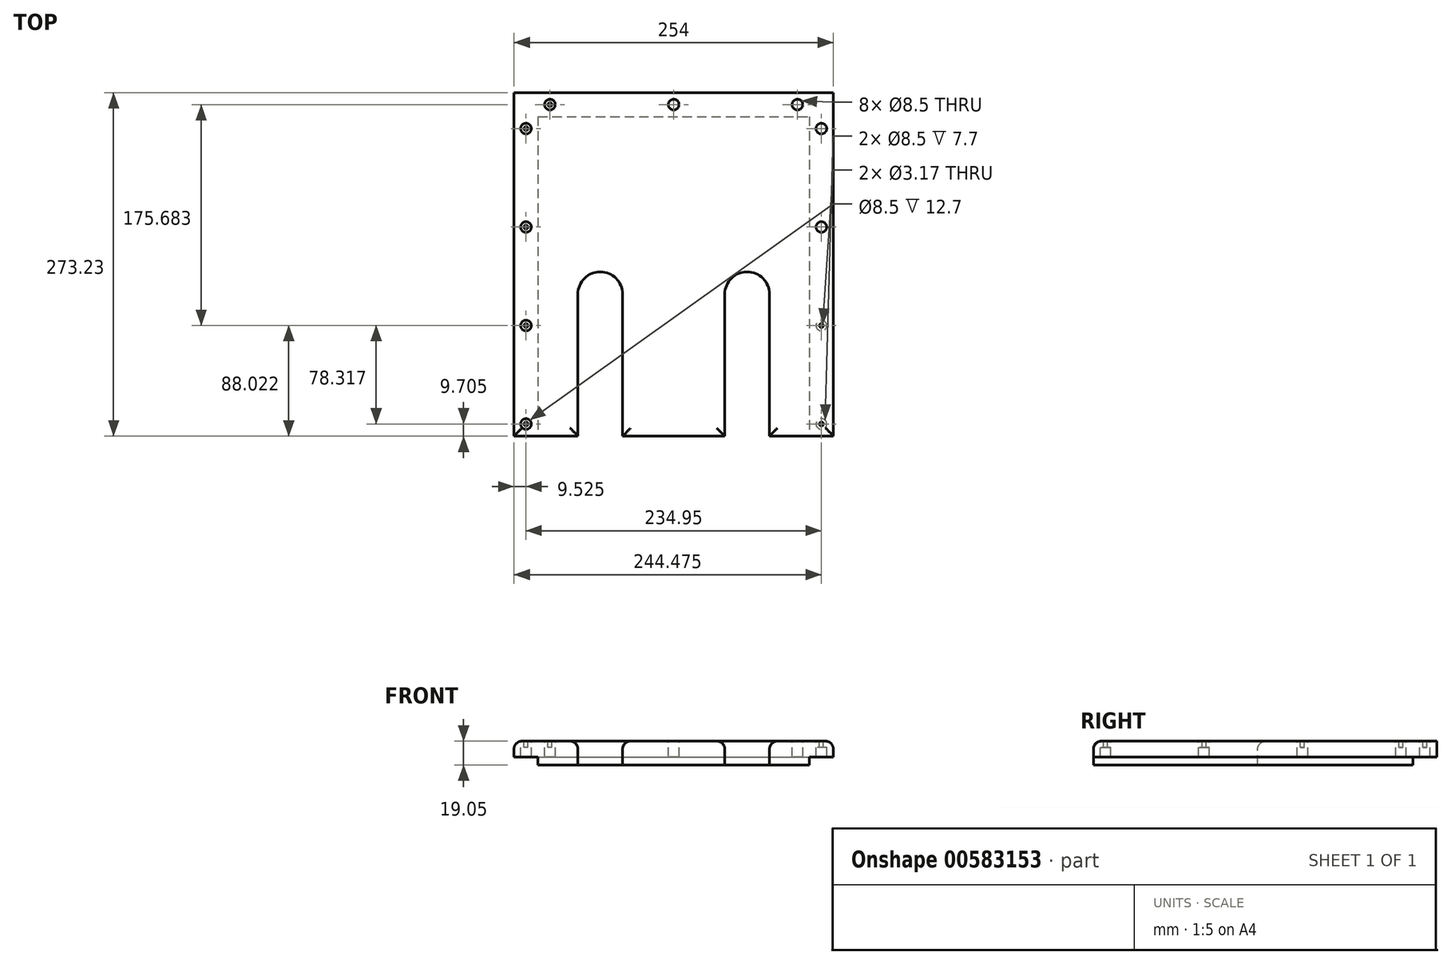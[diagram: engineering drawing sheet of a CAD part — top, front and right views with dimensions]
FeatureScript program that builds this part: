
annotation { "Feature Type Name" : "Feature", "Feature Type Description" : "" }
export const myFeature = defineFeature(function(context is Context, id is Id, definition is map)
    precondition{}
    {
        {
            var Q0;
            Q0=qCreatedBy(makeId("Top.planeOp"),FACE);
            var sketch = newSketch(context, id + "F0", { "sketchPlane" : qUnion([Q0])});
            skCircle(sketch, "E0.MirrorC", {"center": v(28.58, 26.03) * mm, "radius": 1.59 * mm});
            skCircle(sketch, "E1.MirrorC", {"center": v(28.57, 104.35) * mm, "radius": 1.59 * mm});
            skCircle(sketch, "E2.MirrorC", {"center": v(28.57, 182.67) * mm, "radius": 1.59 * mm});
            skCircle(sketch, "E3.MirrorC", {"center": v(28.58, 260.98) * mm, "radius": 1.59 * mm});
            skCircle(sketch, "E4.MirrorC", {"center": v(47.63, 280.03) * mm, "radius": 1.59 * mm});
            skCircle(sketch, "E5.MirrorC", {"center": v(146.05, 280.03) * mm, "radius": 1.59 * mm});
            skLineSegment(sketch, "E6", {"start": v(19.05, 16.5) * mm, "end": v(69.85, 16.5) * mm});
            skLineSegment(sketch, "E7", {"start": v(19.05, 16.5) * mm, "end": v(19.05, 289.56) * mm});
            skLineSegment(sketch, "E8", {"start": v(69.85, 16.5) * mm, "end": v(69.85, 129.3) * mm});
            skLineSegment(sketch, "E9", {"start": v(105.4, 129.3) * mm, "end": v(105.4, 16.33) * mm});
            skLineSegment(sketch, "E10", {"start": v(38.1, 270.5) * mm, "end": v(38.1, 16.5) * mm});
            skArc(sketch, "E11", {"start": v(105.4, 129.3) * mm, "mid": v(87.63, 147.07) * mm, "end": v(69.85, 129.3) * mm});
            skCircle(sketch, "E12", {"center": v(28.58, 26.03) * mm, "radius": 4.25 * mm});
            skCircle(sketch, "E13", {"center": v(28.57, 104.35) * mm, "radius": 4.25 * mm});
            skCircle(sketch, "E14", {"center": v(28.57, 182.67) * mm, "radius": 4.25 * mm});
            skCircle(sketch, "E15", {"center": v(28.58, 260.98) * mm, "radius": 4.25 * mm});
            skCircle(sketch, "E16", {"center": v(47.63, 280.03) * mm, "radius": 4.25 * mm});
            skCircle(sketch, "E17", {"center": v(146.05, 280.03) * mm, "radius": 4.25 * mm});
            skCircle(sketch, "E18.MirrorC", {"center": v(263.53, 182.67) * mm, "radius": 4.25 * mm});
            skCircle(sketch, "E19.MirrorC", {"center": v(244.48, 280.03) * mm, "radius": 4.25 * mm});
            skCircle(sketch, "E20.MirrorC", {"center": v(244.48, 280.03) * mm, "radius": 1.59 * mm});
            skCircle(sketch, "E21.MirrorC", {"center": v(263.53, 260.98) * mm, "radius": 4.25 * mm});
            skCircle(sketch, "E22.MirrorC", {"center": v(263.53, 26.03) * mm, "radius": 1.59 * mm});
            skCircle(sketch, "E23.MirrorC", {"center": v(263.53, 104.35) * mm, "radius": 1.59 * mm});
            skCircle(sketch, "E24.MirrorC", {"center": v(263.53, 26.03) * mm, "radius": 4.25 * mm});
            skCircle(sketch, "E25.MirrorC", {"center": v(263.53, 260.98) * mm, "radius": 1.59 * mm});
            skCircle(sketch, "E26.MirrorC", {"center": v(263.53, 182.67) * mm, "radius": 1.59 * mm});
            skCircle(sketch, "E27.MirrorC", {"center": v(263.53, 104.35) * mm, "radius": 4.25 * mm});
            skLineSegment(sketch, "E28.MirrorCS", {"start": v(273.05, 16.5) * mm, "end": v(222.25, 16.5) * mm});
            skLineSegment(sketch, "E29.MirrorCS", {"start": v(222.25, 16.5) * mm, "end": v(222.25, 129.3) * mm});
            skLineSegment(sketch, "E30.MirrorCS", {"start": v(254, 270.5) * mm, "end": v(254, 16.5) * mm});
            skLineSegment(sketch, "E31.MirrorCS", {"start": v(186.7, 129.3) * mm, "end": v(186.7, 16.33) * mm});
            skLineSegment(sketch, "E32.MirrorCS", {"start": v(273.05, 16.5) * mm, "end": v(273.05, 289.56) * mm});
            skArc(sketch, "E33.MirrorCS", {"start": v(186.7, 129.3) * mm, "mid": v(204.47, 147.07) * mm, "end": v(222.25, 129.3) * mm});
            skLineSegment(sketch, "E34", {"start": v(38.1, 270.5) * mm, "end": v(254, 270.5) * mm});
            skLineSegment(sketch, "E35", {"start": v(19.05, 289.56) * mm, "end": v(273.05, 289.56) * mm});
            skLineSegment(sketch, "E36", {"start": v(105.4, 16.33) * mm, "end": v(186.7, 16.33) * mm});
            skSolve(sketch);
        }
        {
            var Q0;
            {var subQ1=sQuery(id+"F0.wireOp",EDGE,"E8");Q0=makeQuery(id+"F0.imprint","IMPRINT",FACE,{"disambiguationData":[TD([[makeQuery(id+"F0.imprint","IMPRINT",EDGE,{"derivedFrom":subQ1}),1.0]])]});}
            extrude(context, id + "F1", {"entities" : qUnion([Q0]), "depth" : -19.05 * mm, "offsetDistance" : 25 * mm});
        }
        {
            var Q0;
            {var subQ0=sQuery(id+"F0.wireOp",EDGE,"E7");Q0=makeQuery(id+"F0.imprint","IMPRINT",FACE,{"disambiguationData":[TD([[makeQuery(id+"F0.imprint","IMPRINT",EDGE,{"derivedFrom":subQ0}),-1.0]])]});}
            extrude(context, id + "F2", {"entities" : qUnion([Q0]), "operationType" : NewBodyOperationType.ADD, "depth" : -12.7 * mm, "offsetDistance" : 25 * mm});
        }
        {
            var Q0;
            Q0=makeQuery(id+"F0.imprint","IMPRINT",FACE,{"disambiguationData":[TD([[makeQuery(id+"F0.imprint","IMPRINT",EDGE,{"derivedFrom":sQuery(id+"F0.wireOp",EDGE,"E22.MirrorC")}),-1.0]])]});
            var Q1;
            Q1=makeQuery(id+"F0.imprint","IMPRINT",FACE,{"disambiguationData":[TD([[makeQuery(id+"F0.imprint","IMPRINT",EDGE,{"derivedFrom":sQuery(id+"F0.wireOp",EDGE,"E23.MirrorC")}),-1.0]])]});
            var Q2;
            Q2=makeQuery(id+"F0.imprint","IMPRINT",FACE,{"disambiguationData":[TD([[makeQuery(id+"F0.imprint","IMPRINT",EDGE,{"derivedFrom":sQuery(id+"F0.wireOp",EDGE,"E18.MirrorC")}),-1.0]])]});
            var Q3;
            Q3=makeQuery(id+"F0.imprint","IMPRINT",FACE,{"disambiguationData":[TD([[makeQuery(id+"F0.imprint","IMPRINT",EDGE,{"derivedFrom":sQuery(id+"F0.wireOp",EDGE,"E21.MirrorC")}),-1.0]])]});
            var Q4;
            Q4=makeQuery(id+"F0.imprint","IMPRINT",FACE,{"disambiguationData":[TD([[makeQuery(id+"F0.imprint","IMPRINT",EDGE,{"derivedFrom":sQuery(id+"F0.wireOp",EDGE,"E19.MirrorC")}),-1.0]])]});
            var Q5;
            Q5=makeQuery(id+"F0.imprint","IMPRINT",FACE,{"disambiguationData":[TD([[makeQuery(id+"F0.imprint","IMPRINT",EDGE,{"derivedFrom":sQuery(id+"F0.wireOp",EDGE,"E17")}),-1.0]])]});
            var Q6;
            Q6=makeQuery(id+"F0.imprint","IMPRINT",FACE,{"disambiguationData":[TD([[makeQuery(id+"F0.imprint","IMPRINT",EDGE,{"derivedFrom":sQuery(id+"F0.wireOp",EDGE,"E4.MirrorC")}),1.0]])]});
            var Q7;
            Q7=makeQuery(id+"F0.imprint","IMPRINT",FACE,{"disambiguationData":[TD([[makeQuery(id+"F0.imprint","IMPRINT",EDGE,{"derivedFrom":sQuery(id+"F0.wireOp",EDGE,"E3.MirrorC")}),1.0]])]});
            var Q8;
            Q8=makeQuery(id+"F0.imprint","IMPRINT",FACE,{"disambiguationData":[TD([[makeQuery(id+"F0.imprint","IMPRINT",EDGE,{"derivedFrom":sQuery(id+"F0.wireOp",EDGE,"E2.MirrorC")}),1.0]])]});
            var Q9;
            Q9=makeQuery(id+"F0.imprint","IMPRINT",FACE,{"disambiguationData":[TD([[makeQuery(id+"F0.imprint","IMPRINT",EDGE,{"derivedFrom":sQuery(id+"F0.wireOp",EDGE,"E1.MirrorC")}),1.0]])]});
            var Q10;
            Q10=makeQuery(id+"F0.imprint","IMPRINT",FACE,{"disambiguationData":[TD([[makeQuery(id+"F0.imprint","IMPRINT",EDGE,{"derivedFrom":sQuery(id+"F0.wireOp",EDGE,"E0.MirrorC")}),1.0]])]});
            extrude(context, id + "F3", {"entities" : qUnion([Q0, Q1, Q2, Q3, Q4, Q5, Q6, Q7, Q8, Q9, Q10]), "operationType" : NewBodyOperationType.ADD, "depth" : -5 * mm, "offsetDistance" : 25 * mm});
        }
        {
            var Q0;
            Q0=makeQuery(id+"F2.opExtrude","CAP_EDGE",EDGE,{"disambiguationData":[OSD([sQuery(id+"F0.wireOp",EDGE,"E7")])],"isStart":true});
            var Q1;
            {var subQ0=sQuery(id+"F0.wireOp",EDGE,"E6");Q1=makeQuery(id+"F2.boolean.opBoolean","MERGE",EDGE,{"derivedFrom":[makeQuery(id+"F1.opExtrude","CAP_EDGE",EDGE,{"disambiguationData":[OSD([subQ0])],"isStart":true}),makeQuery(id+"F2.opExtrude","CAP_EDGE",EDGE,{"disambiguationData":[OSD([subQ0])],"isStart":true})]});}
            var Q2;
            Q2=makeQuery(id+"F1.opExtrude","CAP_EDGE",EDGE,{"disambiguationData":[OSD([sQuery(id+"F0.wireOp",EDGE,"E8")])],"isStart":true});
            var Q3;
            Q3=makeQuery(id+"F1.opExtrude","CAP_EDGE",EDGE,{"disambiguationData":[OSD([sQuery(id+"F0.wireOp",EDGE,"E36")])],"isStart":true});
            var Q4;
            Q4=makeQuery(id+"F1.opExtrude","CAP_EDGE",EDGE,{"disambiguationData":[OSD([sQuery(id+"F0.wireOp",EDGE,"E31.MirrorCS")])],"isStart":true});
            var Q5;
            {var subQ0=sQuery(id+"F0.wireOp",EDGE,"E28.MirrorCS");Q5=makeQuery(id+"F2.boolean.opBoolean","MERGE",EDGE,{"derivedFrom":[makeQuery(id+"F1.opExtrude","CAP_EDGE",EDGE,{"disambiguationData":[OSD([subQ0])],"isStart":true}),makeQuery(id+"F2.opExtrude","CAP_EDGE",EDGE,{"disambiguationData":[OSD([subQ0])],"isStart":true})]});}
            var Q6;
            Q6=makeQuery(id+"F2.opExtrude","CAP_EDGE",EDGE,{"disambiguationData":[OSD([sQuery(id+"F0.wireOp",EDGE,"E32.MirrorCS")])],"isStart":true});
            fillet(context, id + "F4", {"entities" : qUnion([Q0, Q1, Q2, Q3, Q4, Q5, Q6]), "radius" : 6.35 * mm, "tangentPropagation" : true, "allowEdgeOverflow" : false});
        }
    });
